# Revit family: Armor Large Input AWH
name_source: partatom
category: Mechanical Equipment
revit_build: Autodesk Revit 2015 (Build: 20140606_1530(x64)
units: mm (PartAtom-declared; Revit-internal decimal feet)

## types (5) — shared parameters
# of Electrical Connections = 1
Back Clearance Depth = 24"
Clearance Display = Yes
Condensate Drain Offset From Bottom = 4"
Condensate Drain Offset From Left = 6"
Condensate Drain Radius = 3/8"
Description = Armor Large Input Condensing Commercial Gas Water Heater
FUEL TYPE = NATURAL GAS
Front Clearance Depth = 36"
Fuel Type = Natural or LP
Left Clearance Depth = 24"
Manufacturer = Lochinvar
Outside Gas Conn Offset from Bottom = 14"
Outside Gas Conn Offset from Front = 5"
Right Clearance Depth = 24"
SES BIM Studio # = 18 0649 01
URL = http://www.lochinvar.com
Voltage/Control = 24

## per-type parameters (varying)
- AWH1250NPM: AIR INLET SIZE=6"; A_HEIGHT=51 1/2"; Air Inlet Radius=3"; B_WIDTH=34"; C_DEPTH=49"; D_Unit Depth plus Water Outlet Length=59"; E_Gas Conn Offset from Front=5 1/2"; Elec Conn Offset from Bottom=31 1/2"; Elec Conn Offset from Right=14 1/4"; FLOW RATE (GPM)=112; FRICTION LOSS (FT HD)=23; F_Gas Conn Offset From Left=5 1/2"; Flue Radius=3"; GALLON CAPACITY=11.0; GAS CONN SIZE=1 1/2"; G_Air Inlet Offset From Front=13 1/2"; Gas Conn Radius=3/4"; H_Air Inlet Offset From Left=6 3/4"; INPUT RATE (BTUH)=1,250,000; I_Water Conn Offset from Bottom=46 3/4"; J_Water Inlet Offset from Right=5 3/4"; K_Flue Offset From Left=19 3/4"; L_Flue Offset From Bottom=23"; M_Water Outlet Offset From Right=22 1/2"; VENT SIZE=6"; Voltage & Phase / Heater=120V / 1ø; Voltage & Phase / Pump=120V / 1ø; WATER CONN SIZE=2 1/2"; WEIGHT=1,519; Water Conn Radius=1 1/4"
- AWH1500NPM: AIR INLET SIZE=6"; A_HEIGHT=51 1/2"; Air Inlet Radius=3"; B_WIDTH=34"; C_DEPTH=52 3/4"; D_Unit Depth plus Water Outlet Length=62 3/4"; E_Gas Conn Offset from Front=4 1/2"; Elec Conn Offset from Bottom=31 1/2"; Elec Conn Offset from Right=14 1/4"; FLOW RATE (GPM)=115; FRICTION LOSS (FT HD)=22; F_Gas Conn Offset From Left=4 1/2"; Flue Radius=3"; GALLON CAPACITY=13.0; GAS CONN SIZE=1 1/2"; G_Air Inlet Offset From Front=13 1/2"; Gas Conn Radius=3/4"; H_Air Inlet Offset From Left=6 3/4"; INPUT RATE (BTUH)=1,500,000; I_Water Conn Offset from Bottom=46 3/4"; J_Water Inlet Offset from Right=5 3/4"; K_Flue Offset From Left=19 3/4"; L_Flue Offset From Bottom=23"; M_Water Outlet Offset From Right=22 1/2"; VENT SIZE=6"; Voltage & Phase / Heater=120V / 1ø; Voltage & Phase / Pump=120V / 1ø; WATER CONN SIZE=2 1/2"; WEIGHT=1,672; Water Conn Radius=1 1/4"
- AWH2000NPM: AIR INLET SIZE=8"; A_HEIGHT=51 1/2"; Air Inlet Radius=4"; B_WIDTH=34"; C_DEPTH=65 1/2"; D_Unit Depth plus Water Outlet Length=75 1/2"; E_Gas Conn Offset from Front=7"; Elec Conn Offset from Bottom=31 1/2"; Elec Conn Offset from Right=15 1/4"; FLOW RATE (GPM)=145; FRICTION LOSS (FT HD)=27; F_Gas Conn Offset From Left=5 3/4"; Flue Radius=4"; GALLON CAPACITY=17.0; GAS CONN SIZE=1 1/2"; G_Air Inlet Offset From Front=14 3/4"; Gas Conn Radius=3/4"; H_Air Inlet Offset From Left=7 1/4"; INPUT RATE (BTUH)=2,000,000; I_Water Conn Offset from Bottom=46 3/4"; J_Water Inlet Offset from Right=6 3/4"; K_Flue Offset From Left=18 3/4"; L_Flue Offset From Bottom=23"; M_Water Outlet Offset From Right=23 1/2"; VENT SIZE=8"; Voltage & Phase / Heater=208V / 3ø; Voltage & Phase / Pump=208V / 3ø; WATER CONN SIZE=2 1/2"; WEIGHT=1,931; Water Conn Radius=1 1/4"
- AWH3000NPM: AIR INLET SIZE=10"; A_HEIGHT=67 1/4"; Air Inlet Radius=5"; B_WIDTH=48 1/4"; C_DEPTH=79 3/4"; D_Unit Depth plus Water Outlet Length=93 3/4"; E_Gas Conn Offset from Front=4 3/4"; Elec Conn Offset from Bottom=38"; Elec Conn Offset from Right=22 3/4"; FLOW RATE (GPM)=270; FRICTION LOSS (FT HD)=24; F_Gas Conn Offset From Left=6 3/4"; Flue Radius=5"; GALLON CAPACITY=25.0; GAS CONN SIZE=2"; G_Air Inlet Offset From Front=17 3/4"; Gas Conn Radius=1"; H_Air Inlet Offset From Left=8 3/4"; INPUT RATE (BTUH)=3,000,000; I_Water Conn Offset from Bottom=60 1/4"; J_Water Inlet Offset from Right=8 1/2"; K_Flue Offset From Left=25 1/2"; L_Flue Offset From Bottom=29 1/2"; M_Water Outlet Offset From Right=40"; VENT SIZE=10"; Voltage & Phase / Heater=208V / 3ø; Voltage & Phase / Pump=208V / 3ø; WATER CONN SIZE=4"; WEIGHT=3,147; Water Conn Radius=2"
- AWH4000NPM: AIR INLET SIZE=12"; A_HEIGHT=67 1/4"; Air Inlet Radius=6"; B_WIDTH=48 1/4"; C_DEPTH=96"; D_Unit Depth plus Water Outlet Length=110"; E_Gas Conn Offset from Front=5"; Elec Conn Offset from Bottom=38"; Elec Conn Offset from Right=22 3/4"; FLOW RATE (GPM)=290; FRICTION LOSS (FT HD)=19; F_Gas Conn Offset From Left=7 1/2"; Flue Radius=6"; GALLON CAPACITY=41.0; GAS CONN SIZE=2 1/2"; G_Air Inlet Offset From Front=17 3/4"; Gas Conn Radius=1 1/4"; H_Air Inlet Offset From Left=8 3/4"; INPUT RATE (BTUH)=4,000,000; I_Water Conn Offset from Bottom=60 1/4"; J_Water Inlet Offset from Right=8 1/2"; K_Flue Offset From Left=25 1/2"; L_Flue Offset From Bottom=29 1/2"; M_Water Outlet Offset From Right=40"; VENT SIZE=12"; Voltage & Phase / Heater=480V / 3ø; Voltage & Phase / Pump=480V / 3ø; WATER CONN SIZE=4"; WEIGHT=3,694; Water Conn Radius=2"

note: column(s) folded — value = type name in every type: MODEL NO., Model

## geometry (parser evidence)
native form markers: Sweep x1
no freeform markers — native parametric forms only
